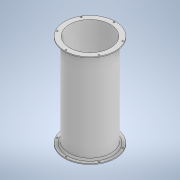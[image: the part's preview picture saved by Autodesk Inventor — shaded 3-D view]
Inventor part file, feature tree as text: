
AUTODESK INVENTOR PART (.ipt)
format: ipt  version: 2021 (Build 250183000, 183)  size: 157,696 bytes
history: native  units: mm
features: revolve x1, hole x1, mirror x1, sketch x1, projected_geometry x1
ambient origin geometry x8: Origin, YZ Plane, XZ Plane, XY Plane, X Axis, Y Axis, Z Axis, Center Point
bodies: Solid1 (feature_tree)
feature tree (5):
  revolve  "Revolution1"  Angle=90.0deg
  hole  "Hole1"  [1 undecoded]
  mirror  "Mirror1"
  sketch  "Sketch2"  dims[d0=300.0mm d3=90.0deg d5=81.5mm d6=2.0mm d7=9.0mm d8=5.0mm d9=45.0deg d10=16.0mm d11=3.0mm d12=3.0mm d13=9.0mm d14=45.0deg d15=5.0mm d16=4.5mm d17=8.0mm d18=60.0mm d20=360.0deg d22=4.5mm d23=10.0mm d24=9.4mm d25=2.0mm d26=90.0deg d27=13.0mm d28=20.594885mm d29=4.5mm]
  projected_geometry  "Projected Loop1"
note: 1 required parameter value undecoded (feature->parameter linkage not recoverable at this tier; creation-order binding heuristic only, values carry confidence <= 0.55)
